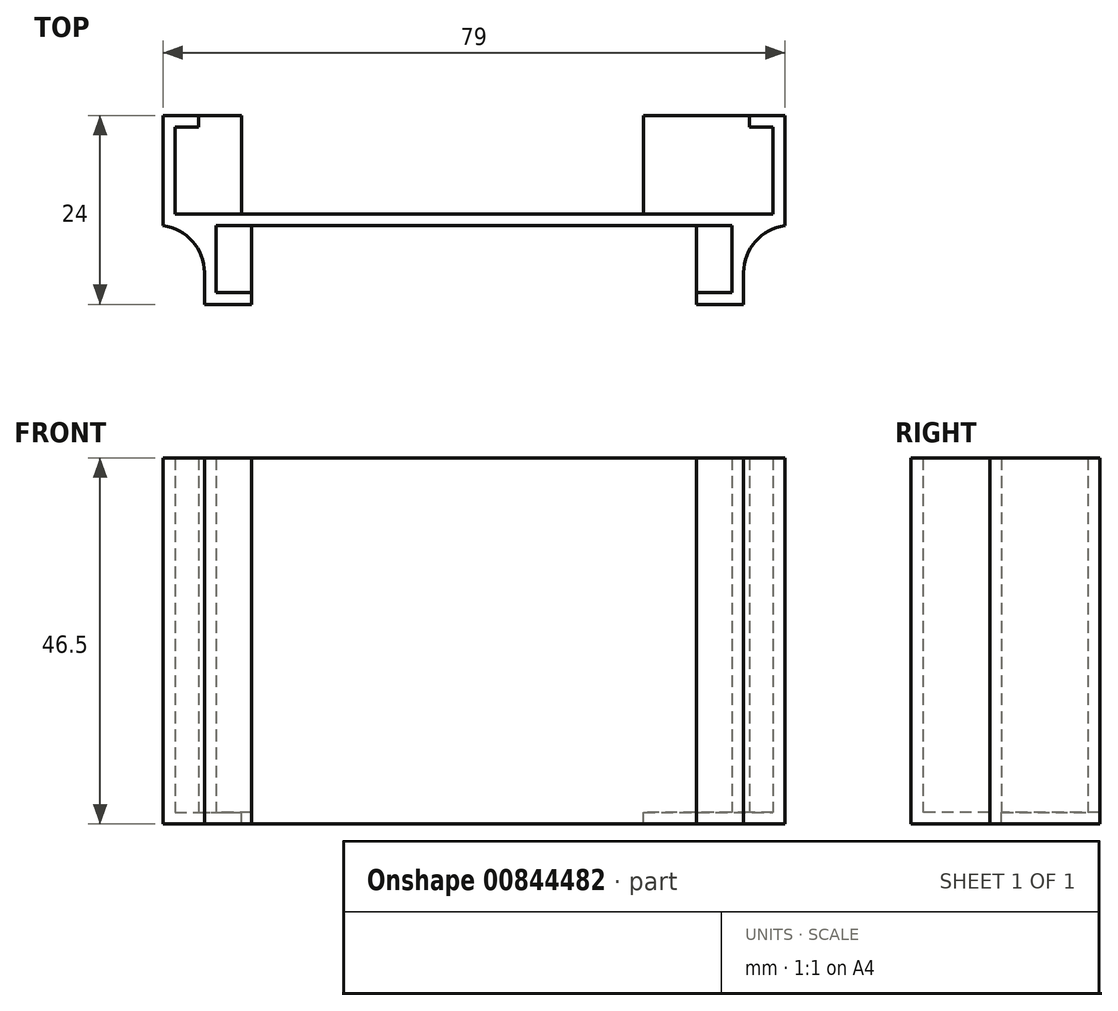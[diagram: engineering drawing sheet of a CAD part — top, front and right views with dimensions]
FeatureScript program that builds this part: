
annotation { "Feature Type Name" : "Feature", "Feature Type Description" : "" }
export const myFeature = defineFeature(function(context is Context, id is Id, definition is map)
    precondition{}
    {
        {
            var Q0;
            Q0=qCreatedBy(makeId("Top.planeOp"),FACE);
            var sketch = newSketch(context, id + "F0", { "sketchPlane" : qUnion([Q0])});
            skLineSegment(sketch, "E0", {"start": v(0, 0) * mm, "end": v(-38, 0) * mm});
            skLineSegment(sketch, "E1", {"start": v(-38, 0) * mm, "end": v(-38, 11) * mm});
            skLineSegment(sketch, "E2", {"start": v(-38, 11) * mm, "end": v(-35, 11) * mm});
            skLineSegment(sketch, "E3.0", {"start": v(-39.5, 12.5) * mm, "end": v(-35, 12.5) * mm});
            skLineSegment(sketch, "E3.1", {"start": v(-39.5, -1.5) * mm, "end": v(-39.5, 12.5) * mm});
            skLineSegment(sketch, "E3.2", {"start": v(0, -1.5) * mm, "end": v(-39.5, -1.5) * mm});
            skLineSegment(sketch, "E4", {"start": v(-35, 12.5) * mm, "end": v(-35, 11) * mm});
            skLineSegment(sketch, "E5.MirrorCS", {"start": v(0, 0) * mm, "end": v(38, 0) * mm});
            skLineSegment(sketch, "E6.MirrorCS", {"start": v(38, 0) * mm, "end": v(38, 11) * mm});
            skLineSegment(sketch, "E7.MirrorCS", {"start": v(38, 11) * mm, "end": v(35, 11) * mm});
            skLineSegment(sketch, "E8.MirrorCS", {"start": v(35, 12.5) * mm, "end": v(35, 11) * mm});
            skLineSegment(sketch, "E9.MirrorCS", {"start": v(39.5, 12.5) * mm, "end": v(35, 12.5) * mm});
            skLineSegment(sketch, "E10.MirrorCS", {"start": v(39.5, -1.5) * mm, "end": v(39.5, 12.5) * mm});
            skLineSegment(sketch, "E11.MirrorCS", {"start": v(0, -1.5) * mm, "end": v(39.5, -1.5) * mm});
            skLineSegment(sketch, "E12", {"start": v(-32.75, -1.5) * mm, "end": v(-32.75, -10) * mm});
            skLineSegment(sketch, "E13", {"start": v(-32.75, -10) * mm, "end": v(-28.25, -10) * mm});
            skLineSegment(sketch, "E14.0", {"start": v(-34.25, -11.5) * mm, "end": v(-28.25, -11.5) * mm});
            skLineSegment(sketch, "E14.1", {"start": v(-34.25, -1.5) * mm, "end": v(-34.25, -11.5) * mm});
            skLineSegment(sketch, "E15", {"start": v(-28.25, -10) * mm, "end": v(-28.25, -11.5) * mm});
            skLineSegment(sketch, "E16.MirrorCS", {"start": v(34.25, -1.5) * mm, "end": v(34.25, -11.5) * mm});
            skLineSegment(sketch, "E17.MirrorCS", {"start": v(32.75, -1.5) * mm, "end": v(32.75, -10) * mm});
            skLineSegment(sketch, "E18.MirrorCS", {"start": v(32.75, -10) * mm, "end": v(28.25, -10) * mm});
            skLineSegment(sketch, "E19.MirrorCS", {"start": v(34.25, -11.5) * mm, "end": v(28.25, -11.5) * mm});
            skLineSegment(sketch, "E20.MirrorCS", {"start": v(28.25, -10) * mm, "end": v(28.25, -11.5) * mm});
            skSolve(sketch);
        }
        {
            var Q0;
            Q0=makeQuery(id+"F0.imprint","IMPRINT",FACE,{"disambiguationData":[TD([[makeQuery(id+"F0.imprint","IMPRINT",EDGE,{"derivedFrom":sQuery(id+"F0.wireOp",EDGE,"E0")}),1.0]])]});
            var Q1;
            {var subQ0=sQuery(id+"F0.wireOp",EDGE,"E12");Q1=makeQuery(id+"F0.imprint","IMPRINT",FACE,{"disambiguationData":[TD([[makeQuery(id+"F0.imprint","IMPRINT",EDGE,{"derivedFrom":subQ0}),-1.0]])]});}
            var Q2;
            {var subQ1=sQuery(id+"F0.wireOp",EDGE,"E16.MirrorCS");Q2=makeQuery(id+"F0.imprint","IMPRINT",FACE,{"disambiguationData":[TD([[makeQuery(id+"F0.imprint","IMPRINT",EDGE,{"derivedFrom":subQ1}),-1.0]])]});}
            extrude(context, id + "F1", {"entities" : qUnion([Q0, Q1, Q2]), "depth" : 45 * mm});
        }
        {
            var Q0;
            Q0=makeQuery(id+"F1.opExtrude","SWEPT_EDGE",EDGE,{"disambiguationData":[OSD([sQuery(id+"F0.wireOp",EDGE,"E3.2"),sQuery(id+"F0.wireOp",EDGE,"E14.1")])]});
            var Q1;
            Q1=makeQuery(id+"F1.opExtrude","SWEPT_EDGE",EDGE,{"disambiguationData":[OSD([sQuery(id+"F0.wireOp",EDGE,"E11.MirrorCS"),sQuery(id+"F0.wireOp",EDGE,"E16.MirrorCS")])]});
            fillet(context, id + "F2", {"entities" : qUnion([Q0, Q1]), "radius" : 6 * mm, "tangentPropagation" : true, "allowEdgeOverflow" : false});
        }
        {
            var Q0;
            Q0=makeQuery(id+"F1.opExtrude","CAP_FACE",FACE,{"disambiguationData":[OSD([sQuery(id+"F0.wireOp",EDGE,"E0"),sQuery(id+"F0.wireOp",EDGE,"E1"),sQuery(id+"F0.wireOp",EDGE,"E2"),sQuery(id+"F0.wireOp",EDGE,"E3.0"),sQuery(id+"F0.wireOp",EDGE,"E3.1"),sQuery(id+"F0.wireOp",EDGE,"E3.2"),sQuery(id+"F0.wireOp",EDGE,"E4"),sQuery(id+"F0.wireOp",EDGE,"E5.MirrorCS"),sQuery(id+"F0.wireOp",EDGE,"E6.MirrorCS"),sQuery(id+"F0.wireOp",EDGE,"E7.MirrorCS"),sQuery(id+"F0.wireOp",EDGE,"E8.MirrorCS"),sQuery(id+"F0.wireOp",EDGE,"E9.MirrorCS"),sQuery(id+"F0.wireOp",EDGE,"E10.MirrorCS"),sQuery(id+"F0.wireOp",EDGE,"E11.MirrorCS"),sQuery(id+"F0.wireOp",EDGE,"E12"),sQuery(id+"F0.wireOp",EDGE,"E13"),sQuery(id+"F0.wireOp",EDGE,"E14.0"),sQuery(id+"F0.wireOp",EDGE,"E14.1"),sQuery(id+"F0.wireOp",EDGE,"E15"),sQuery(id+"F0.wireOp",EDGE,"E16.MirrorCS"),sQuery(id+"F0.wireOp",EDGE,"E17.MirrorCS"),sQuery(id+"F0.wireOp",EDGE,"E18.MirrorCS"),sQuery(id+"F0.wireOp",EDGE,"E19.MirrorCS"),sQuery(id+"F0.wireOp",EDGE,"E20.MirrorCS")])],"isStart":true});
            var sketch = newSketch(context, id + "F3", { "sketchPlane" : qUnion([Q0])});
            skLineSegment(sketch, "E21", {"start": v(-28.25, 10) * mm, "end": v(-28.25, 1.5) * mm});
            skLineSegment(sketch, "E22.MirrorCS", {"start": v(28.25, 10) * mm, "end": v(28.25, 1.5) * mm});
            skLineSegment(sketch, "E23", {"start": v(-35, -12.5) * mm, "end": v(-29.5, -12.5) * mm});
            skLineSegment(sketch, "E24", {"start": v(-29.5, -12.5) * mm, "end": v(-29.5, 0) * mm});
            skLineSegment(sketch, "E25", {"start": v(35, -12.5) * mm, "end": v(21.5, -12.5) * mm});
            skLineSegment(sketch, "E26", {"start": v(21.5, -12.5) * mm, "end": v(21.5, 0) * mm});
            skSolve(sketch);
        }
        {
            var Q0;
            {var subQ22=sQuery(id+"F0.wireOp",EDGE,"E1");var subQ27=makeQuery(id+"F1.opExtrude","CAP_EDGE",EDGE,{"disambiguationData":[OSD([subQ22])],"isStart":true});Q0=makeQuery(id+"F3.imprint","IMPRINT",FACE,{"disambiguationData":[TD([[makeQuery(id+"F3.imprint","IMPRINT",EDGE,{"derivedFrom":subQ27}),-1.0]])]});}
            var Q1;
            {var subQ0=sQuery(id+"F3.wireOp",EDGE,"E21");Q1=makeQuery(id+"F3.imprint","IMPRINT",FACE,{"disambiguationData":[TD([[makeQuery(id+"F3.imprint","IMPRINT",EDGE,{"derivedFrom":subQ0}),-1.0]])]});}
            var Q2;
            Q2=makeQuery(id+"F3.imprint","IMPRINT",FACE,{"disambiguationData":[TD([[makeQuery(id+"F3.imprint","IMPRINT",EDGE,{"derivedFrom":sQuery(id+"F3.wireOp",EDGE,"E23")}),1.0]])]});
            var Q3;
            {var subQ0=sQuery(id+"F3.wireOp",EDGE,"E22.MirrorCS");Q3=makeQuery(id+"F3.imprint","IMPRINT",FACE,{"disambiguationData":[TD([[makeQuery(id+"F3.imprint","IMPRINT",EDGE,{"derivedFrom":subQ0}),1.0]])]});}
            var Q4;
            Q4=makeQuery(id+"F3.imprint","IMPRINT",FACE,{"disambiguationData":[TD([[makeQuery(id+"F3.imprint","IMPRINT",EDGE,{"derivedFrom":sQuery(id+"F3.wireOp",EDGE,"E25")}),-1.0]])]});
            extrude(context, id + "F4", {"entities" : qUnion([Q0, Q1, Q2, Q3, Q4]), "operationType" : NewBodyOperationType.ADD, "depth" : 1.5 * mm, "offsetDistance" : 25 * mm});
        }
    });
